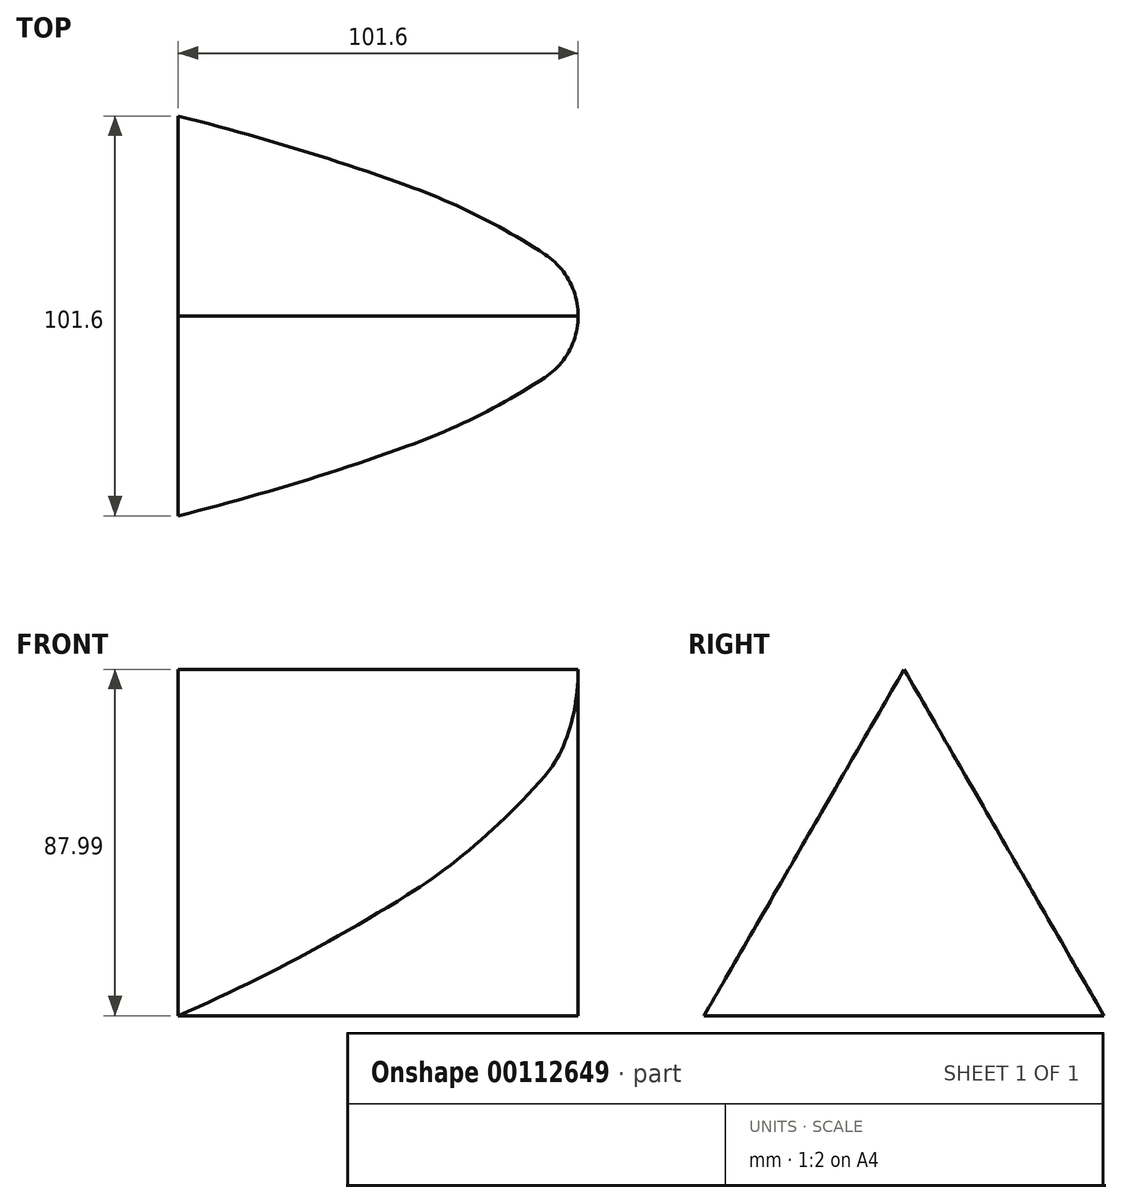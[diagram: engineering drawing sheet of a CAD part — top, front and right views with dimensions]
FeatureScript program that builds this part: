
annotation { "Feature Type Name" : "Feature", "Feature Type Description" : "" }
export const myFeature = defineFeature(function(context is Context, id is Id, definition is map)
    precondition{}
    {
        {
            var Q0;
            Q0=qCreatedBy(makeId("Top.planeOp"),FACE);
            var sketch = newSketch(context, id + "F0", { "sketchPlane" : qUnion([Q0])});
            skLineSegment(sketch, "E0", {"start": v(0, 0) * mm, "end": v(-25.4, 0) * mm, "construction": true});
            skLineSegment(sketch, "E1", {"start": v(0, 0) * mm, "end": v(0, -25.4) * mm, "construction": true});
            skLineSegment(sketch, "E2", {"start": v(0, -25.4) * mm, "end": v(-25.4, -25.4) * mm, "construction": true});
            skLineSegment(sketch, "E3", {"start": v(-25.4, 0) * mm, "end": v(-25.4, -25.4) * mm, "construction": true});
            skArc(sketch, "E4", {"start": v(-8.41, -15.61) * mm, "mid": v(-2.24, -8.87) * mm, "end": v(0, 0) * mm});
            skLineSegment(sketch, "E5", {"start": v(0, 0) * mm, "end": v(-25.4, -25.4) * mm, "construction": true});
            skLineSegment(sketch, "E6", {"start": v(-25.4, -25.4) * mm, "end": v(-50.8, -25.4) * mm, "construction": true});
            skLineSegment(sketch, "E7", {"start": v(-50.8, -25.4) * mm, "end": v(-76.2, -25.4) * mm, "construction": true});
            skLineSegment(sketch, "E8", {"start": v(-76.2, -25.4) * mm, "end": v(-76.2, -50.8) * mm, "construction": true});
            skLineSegment(sketch, "E9", {"start": v(-25.4, -25.4) * mm, "end": v(-76.2, -50.8) * mm, "construction": true});
            skLineSegment(sketch, "E10", {"start": v(0, -25.4) * mm, "end": v(0, -50.8) * mm, "construction": true});
            skLineSegment(sketch, "E11", {"start": v(0, -50.8) * mm, "end": v(-25.4, -50.8) * mm, "construction": true});
            skLineSegment(sketch, "E12", {"start": v(-25.4, -25.4) * mm, "end": v(-25.4, -50.8) * mm, "construction": true});
            skLineSegment(sketch, "E13", {"start": v(-76.2, -25.4) * mm, "end": v(-101.6, -25.4) * mm, "construction": true});
            skLineSegment(sketch, "E14", {"start": v(-101.6, -25.4) * mm, "end": v(-101.6, -50.8) * mm, "construction": true});
            skLineSegment(sketch, "E15", {"start": v(-76.2, -50.8) * mm, "end": v(-50.8, -50.8) * mm, "construction": true});
            skLineSegment(sketch, "E16", {"start": v(-50.8, -50.8) * mm, "end": v(-25.4, -50.8) * mm, "construction": true});
            skLineSegment(sketch, "E17", {"start": v(-76.2, -50.8) * mm, "end": v(-101.6, -50.8) * mm, "construction": true});
            skLineSegment(sketch, "E18", {"start": v(-101.6, -50.8) * mm, "end": v(-127, -50.8) * mm, "construction": true});
            skLineSegment(sketch, "E19", {"start": v(-127, -50.8) * mm, "end": v(-152.4, -50.8) * mm, "construction": true});
            skLineSegment(sketch, "E20", {"start": v(-152.4, -50.8) * mm, "end": v(-177.8, -50.8) * mm, "construction": true});
            skLineSegment(sketch, "E21", {"start": v(-177.8, -50.8) * mm, "end": v(-203.2, -50.8) * mm, "construction": true});
            skLineSegment(sketch, "E22", {"start": v(-203.2, -50.8) * mm, "end": v(-203.2, -76.2) * mm, "construction": true});
            skLineSegment(sketch, "E23", {"start": v(-101.6, -50.8) * mm, "end": v(-203.2, -76.2) * mm, "construction": true});
            skArc(sketch, "E24", {"start": v(-101.6, -50.8) * mm, "mid": v(-72.29, -42.69) * mm, "end": v(-43.42, -33.11) * mm});
            skArc(sketch, "E25", {"start": v(-43.42, -33.11) * mm, "mid": v(-25.4, -25.4) * mm, "end": v(-8.41, -15.61) * mm});
            skLineSegment(sketch, "E26", {"start": v(0, 0) * mm, "end": v(-101.6, 0) * mm});
            skLineSegment(sketch, "E27", {"start": v(-101.6, -50.8) * mm, "end": v(-101.6, 0) * mm});
            skArc(sketch, "E28", {"start": v(0, 0) * mm, "mid": v(-2.24, 8.87) * mm, "end": v(-8.41, 15.61) * mm});
            skArc(sketch, "E29", {"start": v(-8.41, 15.61) * mm, "mid": v(-25.4, 25.4) * mm, "end": v(-43.42, 33.11) * mm});
            skLineSegment(sketch, "E30", {"start": v(-25.4, 0) * mm, "end": v(-25.4, 25.4) * mm, "construction": true});
            skArc(sketch, "E31", {"start": v(-43.42, 33.11) * mm, "mid": v(-72.29, 42.69) * mm, "end": v(-101.6, 50.8) * mm});
            skLineSegment(sketch, "E32", {"start": v(-101.6, 0) * mm, "end": v(-101.6, 50.8) * mm});
            skSolve(sketch);
        }
        {
            var Q0;
            Q0=makeQuery(id+"F0.imprint","IMPRINT",FACE,{"disambiguationData":[TD([[makeQuery(id+"F0.imprint","IMPRINT",EDGE,{"derivedFrom":sQuery(id+"F0.wireOp",EDGE,"E4")}),1.0]])]});
            var Q1;
            Q1=makeQuery(id+"F0.imprint","IMPRINT",FACE,{"disambiguationData":[TD([[makeQuery(id+"F0.imprint","IMPRINT",EDGE,{"derivedFrom":sQuery(id+"F0.wireOp",EDGE,"E26")}),-1.0]])]});
            extrude(context, id + "F1", {"entities" : qUnion([Q0, Q1]), "depth" : 87.99 * mm});
        }
        {
            var Q0;
            Q0=makeQuery(id+"F1.opExtrude","SWEPT_FACE",FACE,{"disambiguationData":[OSD([sQuery(id+"F0.wireOp",EDGE,"E27"),sQuery(id+"F0.wireOp",EDGE,"E32")])]});
            var sketch = newSketch(context, id + "F2", { "sketchPlane" : qUnion([Q0])});
            skLineSegment(sketch, "E33.bottom", {"start": v(-50.8, 87.99) * mm, "end": v(50.8, 87.99) * mm});
            skLineSegment(sketch, "E33.top", {"start": v(-50.8, 0) * mm, "end": v(50.8, 0) * mm, "construction": true});
            skLineSegment(sketch, "E33.left", {"start": v(-50.8, 87.99) * mm, "end": v(-50.8, 0) * mm});
            skLineSegment(sketch, "E33.right", {"start": v(50.8, 87.99) * mm, "end": v(50.8, 0) * mm});
            skLineSegment(sketch, "E34", {"start": v(0, 87.99) * mm, "end": v(50.8, 0) * mm});
            skLineSegment(sketch, "E35", {"start": v(0, 87.99) * mm, "end": v(-50.8, 0) * mm});
            skSolve(sketch);
        }
        {
            var Q0;
            Q0 = qSketchRegion(id + "F2", true);
            var Q1;
            Q1=makeQuery(id+"F1.opExtrude","SWEPT_FACE",FACE,{"disambiguationData":[OSD([sQuery(id+"F0.wireOp",EDGE,"E4"),sQuery(id+"F0.wireOp",EDGE,"E28")])]});
            extrude(context, id + "F3", {"entities" : qUnion([Q0]), "operationType" : NewBodyOperationType.REMOVE, "oppositeDirection" : true, "endBoundEntityFace" : qUnion([Q1]), "depth" : 101.6 * mm});
        }
    });
